# Revit family: Lighting_Outside_Nordlux_Cross-25-Wall
name_source: partatom
category: Lighting Fixtures
revit_build: Autodesk Revit 2018 (Build: 20190510_1515(x64)
units: mm (PartAtom-declared; Revit-internal decimal feet)

## family parameters
Cut with Voids When Loaded = No
Host = Face
Light Source = Yes
OmniClass Number = 23.35.47.11
OmniClass Title = Lighting Fixtures
Part Type = Normal
Room Calculation Point = No
Round Connector Dimension = Use Diameter
Shared = No

## types (2) — shared parameters
Apparent Load = 7 VA
BIMobject category = Outside
Beam angle = 139.50°
CQS = 83.1
CRI / Ra = 83.5
Color Filter = 16777215
Default Elevation = 1219 mm
Description = The round, minimalist design expression of the Cross wall light by Maria Berntsen will embellish any exterior design - almost like a piece of jewellery for your home. Emits a warm, diffused light that creates an inviting atmosphere for your outdoor areas.
Design country = Denmark
Dimming Lamp Color Temperature Shift = <None>
Edition number = 1
Emit Shape Visible in Rendering = No
Emit from Circle Diameter = 80 mm  [stored 0.262467 ft]
Flicker frequency = 102 Hz
IFC Classification = Light Fixture
Installation instructions = https://asset.productmarketingcloud.com
Manufacturer = Nordlux
Manufacturer country = China
Manufacturer name = Nordlux
Material main = Metal
Material secondary = Plastic
Model = Cross 25
NominalVoltage = 230 V
OmniClass Code = 23-35 47 11
OmniClass Description = Lighting Fixtures
Peak [cd] = 61.9
Photometric Web File = Cross 25 Wall Brass.ies
Power factor = 0.54
Product Guid = 0c42a22a-d1c4-4d1b-84d5-163667f891b2
Product SKU = Cross-25-Wall
Product data url = https://bimobject.com
Product family = Lighting
Product group = Wall
Product name = Cross 25 Wall
Product url = https://nordlux.com
QR code = https://bimobject.com
Shade material = Nordlux - Glass - Milky glass
TM30 Rf = 85.3
TM30 Rg = 93.6
Tilt Angle = 90.00°
URL = www.nordlux.com
Weight Net (Kg) = 0,9

## per-type parameters (varying)
| type | Body material | EANNumber |
| ART - (2118131035) Finish colour - (Brass) | Nordlux - Metal - Brass | 2118131035 |
| ART - (2118131003) Finish colour - (Black) | Nordlux - Metal - Black | 2118131003 |

note: [stored X ft] marks values corroborated as IEEE doubles in the binary element streams (Revit-internal decimal feet)

## geometry (parser evidence)
native form markers: Sweep x3
no freeform markers — native parametric forms only
